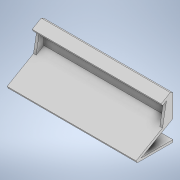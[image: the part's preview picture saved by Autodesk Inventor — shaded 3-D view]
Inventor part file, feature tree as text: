
AUTODESK INVENTOR PART (.ipt)
format: ipt  version: 2020 (Build 240168000, 168)  size: 129,024 bytes
history: native  units: in
note: dims shown in document units (in); Inventor stores cm internally (conversion verified against a paired STEP export)
features: extrude x3, sketch x3
ambient origin geometry x8: Origin, YZ Plane, XZ Plane, XY Plane, X Axis, Y Axis, Z Axis, Center Point
bodies: Solid1 (feature_tree)
feature tree (6):
  extrude  "Extrusion1"  Depth=0.0787in
  extrude  "Extrusion2"  TaperAngle=120.0deg  [1 undecoded]
  extrude  "Extrusion3"  Depth=1.1811in
  sketch  "Sketch1"  dims[d0=0.6693in d1=0.0787in]
  sketch  "Sketch2"  dims[d2=0.315in d3=120.0deg]
  sketch  "Sketch3"  dims[d4=0.0787in d5=1.1811in d6=120.0deg d7=0.0787in d8=3.8583in d9=0.0in d10=0.0787in d11=0.0in d12=0.0787in d13=0.0in]
note: 1 required parameter value undecoded (feature->parameter linkage not recoverable at this tier; creation-order binding heuristic only, values carry confidence <= 0.55)
